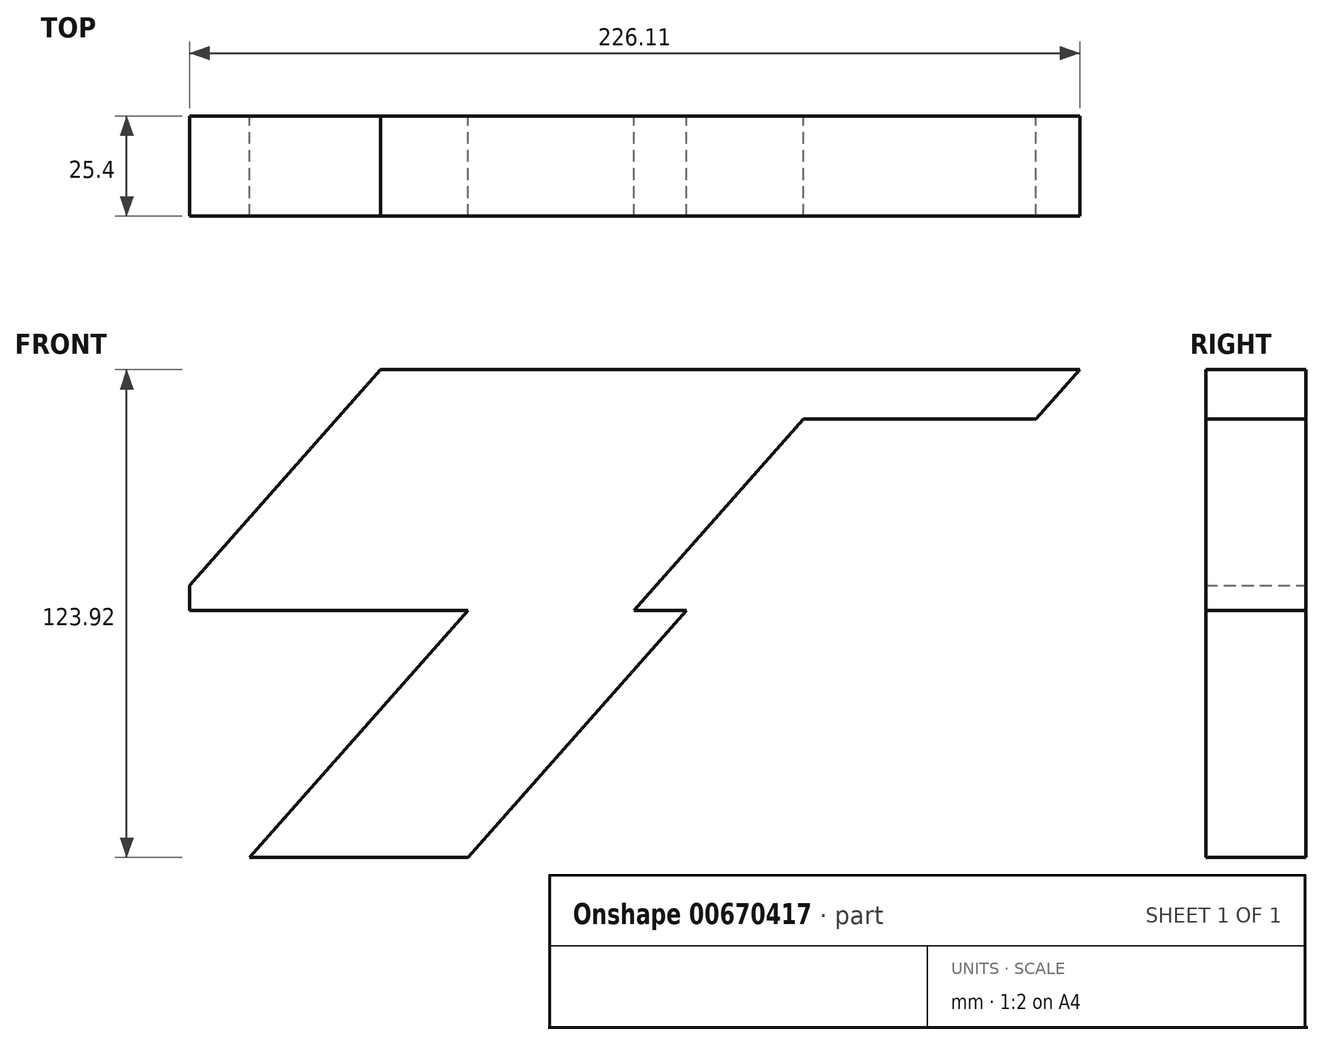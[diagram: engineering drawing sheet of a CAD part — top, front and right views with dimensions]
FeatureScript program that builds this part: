
annotation { "Feature Type Name" : "Feature", "Feature Type Description" : "" }
export const myFeature = defineFeature(function(context is Context, id is Id, definition is map)
    precondition{}
    {
        {
            var Q0;
            Q0=qCreatedBy(makeId("Front.planeOp"),FACE);
            var sketch = newSketch(context, id + "F0", { "sketchPlane" : qUnion([Q0])});
            skLineSegment(sketch, "E0", {"start": v(-112.9, 6.31) * mm, "end": v(-64.39, 61.17) * mm});
            skLineSegment(sketch, "E1", {"start": v(-112.9, 0) * mm, "end": v(-112.9, 6.31) * mm});
            skLineSegment(sketch, "E2", {"start": v(-112.9, 0) * mm, "end": v(-42.23, 0) * mm});
            skLineSegment(sketch, "E3", {"start": v(-64.39, 61.17) * mm, "end": v(0, 61.17) * mm});
            skLineSegment(sketch, "E4", {"start": v(-42.23, 0) * mm, "end": v(-97.71, -62.75) * mm});
            skLineSegment(sketch, "E5", {"start": v(-42.23, -62.75) * mm, "end": v(-97.71, -62.75) * mm});
            skLineSegment(sketch, "E6", {"start": v(-42.23, -62.75) * mm, "end": v(13.26, 0) * mm});
            skLineSegment(sketch, "E7", {"start": v(13.26, 0) * mm, "end": v(0, 0) * mm});
            skLineSegment(sketch, "E8", {"start": v(0, 0) * mm, "end": v(43.01, 48.64) * mm});
            skLineSegment(sketch, "E9", {"start": v(43.01, 48.64) * mm, "end": v(102.12, 48.64) * mm});
            skLineSegment(sketch, "E10", {"start": v(102.12, 48.64) * mm, "end": v(113.2, 61.17) * mm});
            skLineSegment(sketch, "E11", {"start": v(113.2, 61.17) * mm, "end": v(0, 61.17) * mm});
            skSolve(sketch);
        }
        {
            var Q0;
            Q0=makeQuery(id+"F0.imprint","IMPRINT",FACE,{"disambiguationData":[TD([[makeQuery(id+"F0.imprint","IMPRINT",EDGE,{"derivedFrom":sQuery(id+"F0.wireOp",EDGE,"E0")}),-1.0]])]});
            extrude(context, id + "F1", {"entities" : qUnion([Q0]), "depth" : 25.4 * mm, "offsetDistance" : 25.4 * mm});
        }
    });
